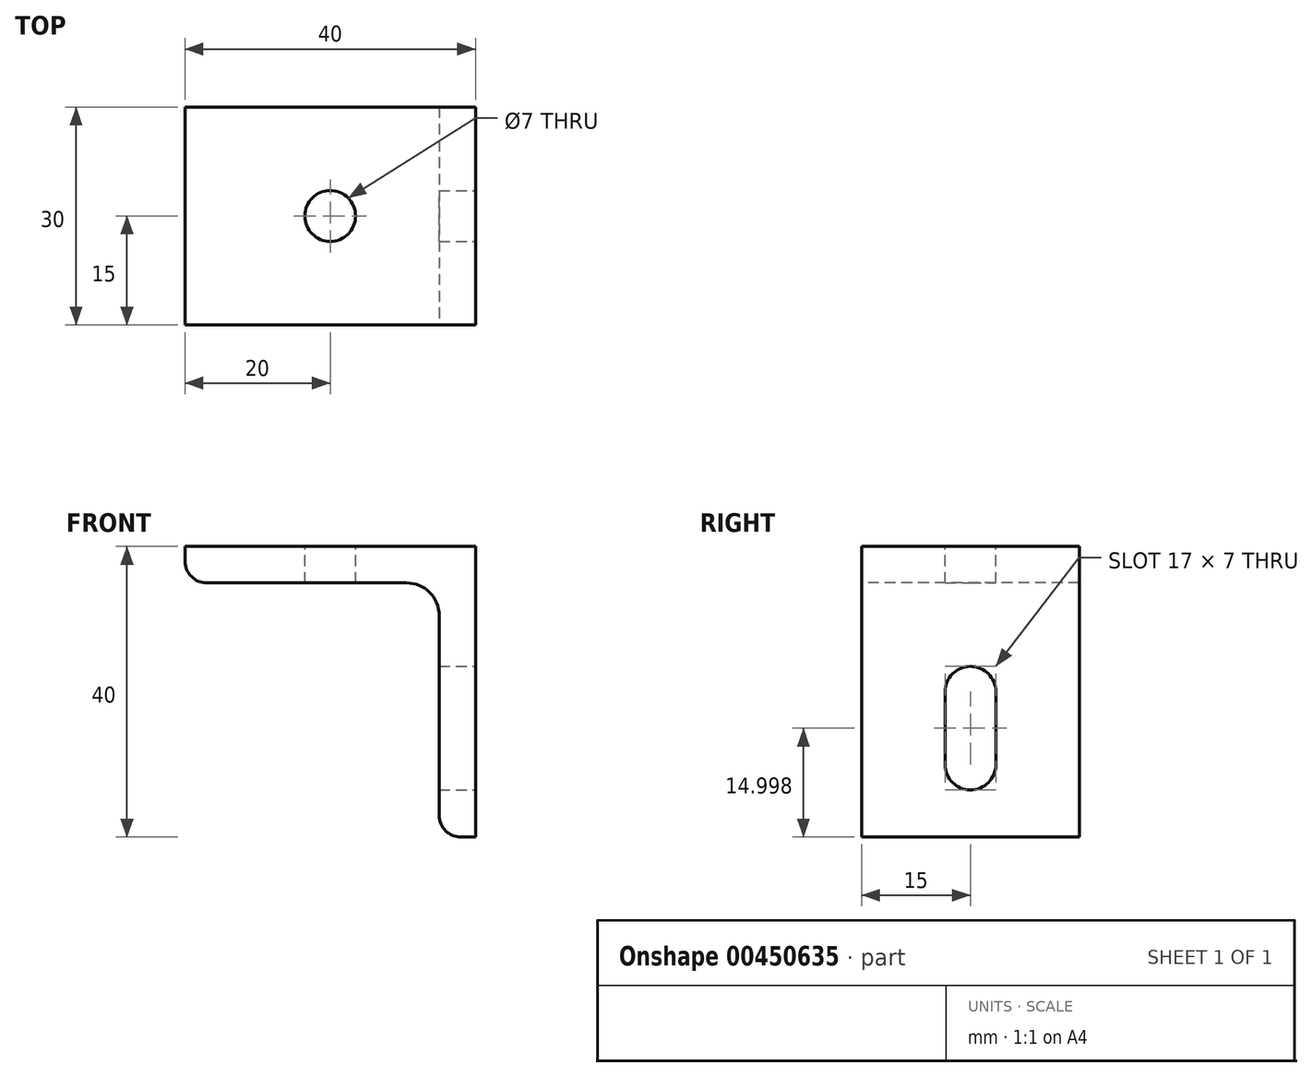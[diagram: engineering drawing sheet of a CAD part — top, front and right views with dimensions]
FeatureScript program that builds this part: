
annotation { "Feature Type Name" : "Feature", "Feature Type Description" : "" }
export const myFeature = defineFeature(function(context is Context, id is Id, definition is map)
    precondition{}
    {
        {
            var Q0;
            Q0=qCreatedBy(makeId("Front.planeOp"),FACE);
            var sketch = newSketch(context, id + "F0", { "sketchPlane" : qUnion([Q0])});
            skLineSegment(sketch, "E0", {"start": v(-170.8, -196.38) * mm, "end": v(99.2, -196.38) * mm});
            skLineSegment(sketch, "E1", {"start": v(-170.8, -169.38) * mm, "end": v(-170.8, -196.38) * mm});
            skLineSegment(sketch, "E2", {"start": v(-170.8, -169.38) * mm, "end": v(99.2, -169.38) * mm});
            skLineSegment(sketch, "E3", {"start": v(-75.8, -192.38) * mm, "end": v(-18.8, -192.38) * mm});
            skLineSegment(sketch, "E4", {"start": v(-75.8, -183.07) * mm, "end": v(-18.8, -183.07) * mm});
            skLineSegment(sketch, "E5", {"start": v(-170.8, -188.38) * mm, "end": v(-75.8, -188.38) * mm});
            skLineSegment(sketch, "E6", {"start": v(-75.8, -169.38) * mm, "end": v(-75.8, -196.38) * mm});
            skLineSegment(sketch, "E7", {"start": v(-36.8, -183.07) * mm, "end": v(-36.8, -196.38) * mm});
            skLineSegment(sketch, "E8", {"start": v(-18.8, -187.38) * mm, "end": v(99.2, -187.38) * mm});
            skLineSegment(sketch, "E9", {"start": v(26.2, -178.38) * mm, "end": v(99.2, -178.38) * mm});
            skLineSegment(sketch, "E10", {"start": v(-18.8, -174.38) * mm, "end": v(26.2, -174.38) * mm});
            skLineSegment(sketch, "E11", {"start": v(24, -176.8) * mm, "end": v(16.58, -185.84) * mm});
            skLineSegment(sketch, "E12", {"start": v(-18.8, -169.38) * mm, "end": v(-18.8, -196.38) * mm});
            skLineSegment(sketch, "E13", {"start": v(-1.8, -169.38) * mm, "end": v(-1.8, -187.38) * mm});
            skLineSegment(sketch, "E14", {"start": v(-17.86, -180.9) * mm, "end": v(-10.14, -180.9) * mm});
            skCircle(sketch, "E15", {"center": v(-14, -180.9) * mm, "radius": 2.97 * mm});
            skCircle(sketch, "E16", {"center": v(-14, -180.9) * mm, "radius": 1.47 * mm});
            skLineSegment(sketch, "E17", {"start": v(-14, -177.04) * mm, "end": v(-14, -184.77) * mm});
            skLineSegment(sketch, "E18", {"start": v(-4.04, -177.93) * mm, "end": v(-4.04, -183.87) * mm});
            skLineSegment(sketch, "E19", {"start": v(-8.12, -179.44) * mm, "end": v(-8.12, -182.37) * mm});
            skLineSegment(sketch, "E20", {"start": v(-4.04, -183.87) * mm, "end": v(-8.12, -182.37) * mm});
            skLineSegment(sketch, "E21", {"start": v(-8.95, -180.9) * mm, "end": v(-3.11, -180.9) * mm});
            skLineSegment(sketch, "E22", {"start": v(-4.04, -177.93) * mm, "end": v(-8.12, -179.44) * mm});
            skLineSegment(sketch, "E23", {"start": v(15.2, -169.38) * mm, "end": v(15.2, -187.38) * mm});
            skLineSegment(sketch, "E24", {"start": v(26.2, -169.38) * mm, "end": v(26.2, -187.38) * mm});
            skLineSegment(sketch, "E25", {"start": v(71.2, -187.38) * mm, "end": v(71.2, -196.38) * mm});
            skLineSegment(sketch, "E26", {"start": v(71.2, -169.38) * mm, "end": v(71.2, -178.38) * mm});
            skLineSegment(sketch, "E27", {"start": v(99.2, -12.38) * mm, "end": v(1.2, -12.38) * mm});
            skLineSegment(sketch, "E28", {"start": v(99.2, -18.38) * mm, "end": v(1.2, -18.38) * mm});
            skLineSegment(sketch, "E29", {"start": v(99.2, -24.38) * mm, "end": v(1.2, -24.38) * mm});
            skLineSegment(sketch, "E30", {"start": v(15.2, -6.38) * mm, "end": v(15.2, -24.38) * mm});
            skLineSegment(sketch, "E31", {"start": v(1.2, -6.38) * mm, "end": v(1.2, -24.38) * mm});
            skLineSegment(sketch, "E32", {"start": v(5.62, -11.28) * mm, "end": v(10.42, -11.28) * mm});
            skLineSegment(sketch, "E33", {"start": v(74.2, -6.38) * mm, "end": v(74.2, -24.38) * mm});
            skLineSegment(sketch, "E34", {"start": v(89.2, -6.38) * mm, "end": v(89.2, -24.38) * mm});
            skLineSegment(sketch, "E35", {"start": v(5.62, -11.28) * mm, "end": v(8.02, -7.28) * mm});
            skLineSegment(sketch, "E36", {"start": v(8.02, -7.28) * mm, "end": v(10.42, -11.28) * mm});
            skLineSegment(sketch, "E37", {"start": v(5.62, -17.28) * mm, "end": v(10.42, -17.28) * mm});
            skLineSegment(sketch, "E38", {"start": v(5.62, -17.28) * mm, "end": v(8.02, -13.28) * mm});
            skLineSegment(sketch, "E39", {"start": v(8.02, -13.28) * mm, "end": v(10.42, -17.28) * mm});
            skLineSegment(sketch, "E40", {"start": v(-170.8, -196.38) * mm, "end": v(-170.8, -6.38) * mm});
            skLineSegment(sketch, "E41", {"start": v(99.2, -196.38) * mm, "end": v(99.2, -6.38) * mm});
            skLineSegment(sketch, "E42", {"start": v(-170.8, -6.38) * mm, "end": v(99.2, -6.38) * mm});
            skLineSegment(sketch, "E43", {"start": v(144.6, -84.48) * mm, "end": v(146.05, -86.98) * mm});
            skLineSegment(sketch, "E44", {"start": v(146.05, -86.98) * mm, "end": v(149.23, -81.48) * mm});
            skLineSegment(sketch, "E45", {"start": v(149.23, -81.48) * mm, "end": v(155.58, -81.48) * mm});
            skLineSegment(sketch, "E46", {"start": v(144.6, -84.48) * mm, "end": v(147.5, -84.48) * mm});
            skLineSegment(sketch, "E47", {"start": v(157.64, -84.48) * mm, "end": v(159.08, -86.98) * mm});
            skLineSegment(sketch, "E48", {"start": v(159.08, -86.98) * mm, "end": v(162.25, -81.48) * mm});
            skCircle(sketch, "E49", {"center": v(159.08, -85.31) * mm, "radius": 0.83 * mm});
            skArc(sketch, "E50", {"start": v(144.43, -81.3) * mm, "mid": v(143.38, -84.23) * mm, "end": v(144.43, -87.15) * mm});
            skArc(sketch, "E51", {"start": v(164.29, -87.15) * mm, "mid": v(165.34, -84.23) * mm, "end": v(164.29, -81.3) * mm});
            skLineSegment(sketch, "E52", {"start": v(136.3, -188.2) * mm, "end": v(146.3, -188.2) * mm});
            skLineSegment(sketch, "E53", {"start": v(146.3, -188.2) * mm, "end": v(146.3, -178.2) * mm});
            skLineSegment(sketch, "E54", {"start": v(146.3, -178.2) * mm, "end": v(136.3, -188.2) * mm});
            skLineSegment(sketch, "E55", {"start": v(155.92, -74.84) * mm, "end": v(157.37, -77.34) * mm});
            skLineSegment(sketch, "E56", {"start": v(157.37, -77.34) * mm, "end": v(160.54, -71.84) * mm});
            skLineSegment(sketch, "E57", {"start": v(160.54, -71.84) * mm, "end": v(167.77, -71.84) * mm});
            skLineSegment(sketch, "E58", {"start": v(155.92, -74.84) * mm, "end": v(158.81, -74.84) * mm});
            skCircle(sketch, "E59", {"center": v(160.54, -71.84) * mm, "radius": 0.79 * mm});
            skLineSegment(sketch, "E60", {"start": v(153.92, -77.34) * mm, "end": v(168.92, -77.34) * mm});
            skLineSegment(sketch, "E61", {"start": v(135.86, -112.96) * mm, "end": v(137.3, -115.46) * mm});
            skLineSegment(sketch, "E62", {"start": v(137.3, -115.46) * mm, "end": v(140.48, -109.96) * mm});
            skLineSegment(sketch, "E63", {"start": v(140.48, -109.96) * mm, "end": v(147.7, -109.96) * mm});
            skLineSegment(sketch, "E64", {"start": v(135.86, -112.96) * mm, "end": v(138.75, -112.96) * mm});
            skLineSegment(sketch, "E65", {"start": v(135.86, -122.83) * mm, "end": v(137.3, -125.33) * mm});
            skLineSegment(sketch, "E66", {"start": v(137.3, -125.33) * mm, "end": v(140.48, -119.83) * mm});
            skLineSegment(sketch, "E67", {"start": v(140.48, -119.83) * mm, "end": v(147.7, -119.83) * mm});
            skLineSegment(sketch, "E68", {"start": v(135.86, -122.83) * mm, "end": v(138.75, -122.83) * mm});
            skLineSegment(sketch, "E69", {"start": v(135.77, -132.54) * mm, "end": v(137.22, -135.04) * mm});
            skLineSegment(sketch, "E70", {"start": v(137.22, -135.04) * mm, "end": v(140.4, -129.54) * mm});
            skLineSegment(sketch, "E71", {"start": v(140.4, -129.54) * mm, "end": v(146.74, -129.54) * mm});
            skLineSegment(sketch, "E72", {"start": v(135.77, -132.54) * mm, "end": v(138.66, -132.54) * mm});
            skLineSegment(sketch, "E73", {"start": v(135.92, -141.53) * mm, "end": v(137.37, -144.03) * mm});
            skLineSegment(sketch, "E74", {"start": v(137.37, -144.03) * mm, "end": v(140.54, -138.53) * mm});
            skLineSegment(sketch, "E75", {"start": v(140.54, -138.53) * mm, "end": v(146.92, -138.53) * mm});
            skLineSegment(sketch, "E76", {"start": v(135.92, -141.53) * mm, "end": v(138.81, -141.53) * mm});
            skLineSegment(sketch, "E77", {"start": v(135.92, -150.24) * mm, "end": v(137.37, -152.74) * mm});
            skLineSegment(sketch, "E78", {"start": v(137.37, -152.74) * mm, "end": v(140.54, -147.24) * mm});
            skLineSegment(sketch, "E79", {"start": v(140.54, -147.24) * mm, "end": v(146.92, -147.24) * mm});
            skLineSegment(sketch, "E80", {"start": v(135.92, -150.24) * mm, "end": v(138.81, -150.24) * mm});
            skLineSegment(sketch, "E81", {"start": v(136.89, -26.68) * mm, "end": v(138.33, -29.18) * mm});
            skLineSegment(sketch, "E82", {"start": v(138.33, -29.18) * mm, "end": v(141.5, -23.68) * mm});
            skLineSegment(sketch, "E83", {"start": v(141.5, -23.68) * mm, "end": v(148.73, -23.68) * mm});
            skLineSegment(sketch, "E84", {"start": v(136.89, -26.68) * mm, "end": v(139.77, -26.68) * mm});
            skLineSegment(sketch, "E85", {"start": v(134.88, -29.18) * mm, "end": v(149.88, -29.18) * mm});
            skLineSegment(sketch, "E86", {"start": v(136.89, -36.55) * mm, "end": v(138.33, -39.05) * mm});
            skLineSegment(sketch, "E87", {"start": v(138.33, -39.05) * mm, "end": v(141.5, -33.55) * mm});
            skLineSegment(sketch, "E88", {"start": v(141.5, -33.55) * mm, "end": v(148.73, -33.55) * mm});
            skLineSegment(sketch, "E89", {"start": v(136.89, -36.55) * mm, "end": v(139.77, -36.55) * mm});
            skLineSegment(sketch, "E90", {"start": v(134.88, -39.05) * mm, "end": v(149.88, -39.05) * mm});
            skLineSegment(sketch, "E91", {"start": v(136.8, -46.27) * mm, "end": v(138.24, -48.77) * mm});
            skLineSegment(sketch, "E92", {"start": v(138.24, -48.77) * mm, "end": v(141.42, -43.27) * mm});
            skLineSegment(sketch, "E93", {"start": v(141.42, -43.27) * mm, "end": v(147.76, -43.27) * mm});
            skLineSegment(sketch, "E94", {"start": v(136.8, -46.27) * mm, "end": v(139.68, -46.27) * mm});
            skLineSegment(sketch, "E95", {"start": v(134.8, -48.77) * mm, "end": v(149.8, -48.77) * mm});
            skLineSegment(sketch, "E96", {"start": v(136.95, -55.25) * mm, "end": v(138.4, -57.75) * mm});
            skLineSegment(sketch, "E97", {"start": v(138.4, -57.75) * mm, "end": v(141.57, -52.25) * mm});
            skLineSegment(sketch, "E98", {"start": v(141.57, -52.25) * mm, "end": v(147.95, -52.25) * mm});
            skLineSegment(sketch, "E99", {"start": v(136.95, -55.25) * mm, "end": v(139.83, -55.25) * mm});
            skLineSegment(sketch, "E100", {"start": v(134.94, -57.75) * mm, "end": v(149.94, -57.75) * mm});
            skLineSegment(sketch, "E101", {"start": v(136.95, -63.96) * mm, "end": v(138.4, -66.46) * mm});
            skLineSegment(sketch, "E102", {"start": v(138.4, -66.46) * mm, "end": v(141.57, -60.96) * mm});
            skLineSegment(sketch, "E103", {"start": v(141.57, -60.96) * mm, "end": v(147.95, -60.96) * mm});
            skLineSegment(sketch, "E104", {"start": v(136.95, -63.96) * mm, "end": v(139.83, -63.96) * mm});
            skLineSegment(sketch, "E105", {"start": v(134.88, -66.36) * mm, "end": v(149.88, -66.36) * mm});
            skLineSegment(sketch, "E106", {"start": v(137.15, -84.48) * mm, "end": v(138.6, -86.98) * mm});
            skLineSegment(sketch, "E107", {"start": v(138.6, -86.98) * mm, "end": v(141.77, -81.48) * mm});
            skLineSegment(sketch, "E108", {"start": v(137.56, -74.63) * mm, "end": v(139, -77.13) * mm});
            skLineSegment(sketch, "E109", {"start": v(139, -77.13) * mm, "end": v(142.18, -71.63) * mm});
            skCircle(sketch, "E110", {"center": v(139, -75.47) * mm, "radius": 0.83 * mm});
            skLineSegment(sketch, "E111", {"start": v(136, -77.13) * mm, "end": v(143, -77.13) * mm});
            skLineSegment(sketch, "E112", {"start": v(146.86, -74.84) * mm, "end": v(148.3, -77.34) * mm});
            skLineSegment(sketch, "E113", {"start": v(148.3, -77.34) * mm, "end": v(151.48, -71.84) * mm});
            skLineSegment(sketch, "E114", {"start": v(146.86, -74.84) * mm, "end": v(149.74, -74.84) * mm});
            skLineSegment(sketch, "E115", {"start": v(145.3, -77.34) * mm, "end": v(152.3, -77.34) * mm});
            skLineSegment(sketch, "E116", {"start": v(136.3, -93.03) * mm, "end": v(137.75, -95.53) * mm});
            skLineSegment(sketch, "E117", {"start": v(137.75, -95.53) * mm, "end": v(140.93, -90.03) * mm});
            skLineSegment(sketch, "E118", {"start": v(141.75, -95.53) * mm, "end": v(134.75, -95.53) * mm});
            skLineSegment(sketch, "E119", {"start": v(157.93, -63.96) * mm, "end": v(159.38, -66.46) * mm});
            skLineSegment(sketch, "E120", {"start": v(159.38, -66.46) * mm, "end": v(162.55, -60.96) * mm});
            skLineSegment(sketch, "E121", {"start": v(162.55, -60.96) * mm, "end": v(168.93, -60.96) * mm});
            skLineSegment(sketch, "E122", {"start": v(157.93, -63.96) * mm, "end": v(160.82, -63.96) * mm});
            skLineSegment(sketch, "E123", {"start": v(155.87, -66.36) * mm, "end": v(170.87, -66.36) * mm});
            skLineSegment(sketch, "E124", {"start": v(157.93, -151.56) * mm, "end": v(159.38, -154.06) * mm});
            skLineSegment(sketch, "E125", {"start": v(159.38, -154.06) * mm, "end": v(162.55, -148.56) * mm});
            skLineSegment(sketch, "E126", {"start": v(162.55, -148.56) * mm, "end": v(168.93, -148.56) * mm});
            skLineSegment(sketch, "E127", {"start": v(157.93, -151.56) * mm, "end": v(160.82, -151.56) * mm});
            skLineSegment(sketch, "E128", {"start": v(145.83, -161.12) * mm, "end": v(147.28, -163.62) * mm});
            skLineSegment(sketch, "E129", {"start": v(147.28, -163.62) * mm, "end": v(150.45, -158.12) * mm});
            skLineSegment(sketch, "E130", {"start": v(145.83, -161.12) * mm, "end": v(148.72, -161.12) * mm});
            skLineSegment(sketch, "E131", {"start": v(136.53, -160.9) * mm, "end": v(137.98, -163.4) * mm});
            skLineSegment(sketch, "E132", {"start": v(137.98, -163.4) * mm, "end": v(141.15, -157.9) * mm});
            skCircle(sketch, "E133", {"center": v(137.98, -161.74) * mm, "radius": 0.83 * mm});
            skLineSegment(sketch, "E134", {"start": v(-72, -178.14) * mm, "end": v(-70.55, -180.64) * mm});
            skLineSegment(sketch, "E135", {"start": v(-70.55, -180.64) * mm, "end": v(-67.37, -175.14) * mm});
            skLineSegment(sketch, "E136", {"start": v(-60.61, -177.93) * mm, "end": v(-59.17, -180.43) * mm});
            skLineSegment(sketch, "E137", {"start": v(-59.17, -180.43) * mm, "end": v(-56, -174.93) * mm});
            skCircle(sketch, "E138", {"center": v(-59.17, -178.76) * mm, "radius": 0.83 * mm});
            skArc(sketch, "E139", {"start": v(-75.97, -110.64) * mm, "mid": v(-77.52, -107.99) * mm, "end": v(-80.4, -106.94) * mm});
            skArc(sketch, "E140", {"start": v(-75.9, -111.44) * mm, "mid": v(-75.92, -111.04) * mm, "end": v(-75.97, -110.64) * mm});
            skLineSegment(sketch, "E141", {"start": v(-80.4, -106.94) * mm, "end": v(-107.9, -106.94) * mm});
            skLineSegment(sketch, "E142", {"start": v(-75.9, -138.94) * mm, "end": v(-75.9, -111.44) * mm});
            skArc(sketch, "E143", {"start": v(-110.9, -103.94) * mm, "mid": v(-110.02, -106.06) * mm, "end": v(-107.9, -106.94) * mm});
            skLineSegment(sketch, "E144", {"start": v(-110.9, -103.94) * mm, "end": v(-110.9, -101.94) * mm});
            skArc(sketch, "E145", {"start": v(-75.9, -138.94) * mm, "mid": v(-75.02, -141.06) * mm, "end": v(-72.9, -141.94) * mm});
            skLineSegment(sketch, "E146", {"start": v(-70.9, -141.94) * mm, "end": v(-72.9, -141.94) * mm});
            skLineSegment(sketch, "E147", {"start": v(-70.9, -141.94) * mm, "end": v(-70.9, -101.94) * mm});
            skLineSegment(sketch, "E148", {"start": v(-70.9, -101.94) * mm, "end": v(-110.9, -101.94) * mm});
            skLineSegment(sketch, "E149", {"start": v(37.15, -106.94) * mm, "end": v(7.15, -106.94) * mm});
            skLineSegment(sketch, "E150", {"start": v(7.15, -139.94) * mm, "end": v(7.15, -101.94) * mm});
            skLineSegment(sketch, "E151", {"start": v(9.15, -141.94) * mm, "end": v(7.15, -139.94) * mm});
            skLineSegment(sketch, "E152", {"start": v(35.15, -141.94) * mm, "end": v(9.15, -141.94) * mm});
            skLineSegment(sketch, "E153", {"start": v(37.15, -139.94) * mm, "end": v(35.15, -141.94) * mm});
            skArc(sketch, "E154", {"start": v(18.65, -131.94) * mm, "mid": v(22.15, -135.44) * mm, "end": v(25.65, -131.94) * mm});
            skArc(sketch, "E155", {"start": v(25.65, -121.94) * mm, "mid": v(22.15, -118.44) * mm, "end": v(18.65, -121.94) * mm});
            skLineSegment(sketch, "E156", {"start": v(17.6, -131.94) * mm, "end": v(26.7, -131.94) * mm});
            skLineSegment(sketch, "E157", {"start": v(17.6, -121.94) * mm, "end": v(26.7, -121.94) * mm});
            skLineSegment(sketch, "E158", {"start": v(18.65, -121.94) * mm, "end": v(18.65, -131.94) * mm});
            skLineSegment(sketch, "E159", {"start": v(25.65, -131.94) * mm, "end": v(25.65, -121.94) * mm});
            skLineSegment(sketch, "E160", {"start": v(37.15, -139.94) * mm, "end": v(37.15, -101.94) * mm});
            skLineSegment(sketch, "E161", {"start": v(7.15, -101.94) * mm, "end": v(37.15, -101.94) * mm});
            skLineSegment(sketch, "E162", {"start": v(-75.9, -55.1) * mm, "end": v(-75.9, -25.1) * mm});
            skLineSegment(sketch, "E163", {"start": v(-108.9, -25.1) * mm, "end": v(-70.9, -25.1) * mm});
            skLineSegment(sketch, "E164", {"start": v(-110.9, -53.1) * mm, "end": v(-110.9, -27.1) * mm});
            skLineSegment(sketch, "E165", {"start": v(-108.9, -25.1) * mm, "end": v(-110.9, -27.1) * mm});
            skLineSegment(sketch, "E166", {"start": v(-108.9, -55.1) * mm, "end": v(-110.9, -53.1) * mm});
            skLineSegment(sketch, "E167", {"start": v(-90.9, -35.56) * mm, "end": v(-90.9, -44.66) * mm});
            skLineSegment(sketch, "E168", {"start": v(-108.9, -55.1) * mm, "end": v(-70.9, -55.1) * mm});
            skLineSegment(sketch, "E169", {"start": v(-70.9, -25.1) * mm, "end": v(-70.9, -55.1) * mm});
            skLineSegment(sketch, "E170", {"start": v(22.15, -117.4) * mm, "end": v(22.15, -136.5) * mm});
            skLineSegment(sketch, "E171", {"start": v(-86.35, -40.1) * mm, "end": v(-95.45, -40.1) * mm});
            skCircle(sketch, "E172", {"center": v(-90.9, -40.1) * mm, "radius": 3.5 * mm});
            skLineSegment(sketch, "E173", {"start": v(-61.22, -99.44) * mm, "end": v(-59.78, -101.94) * mm});
            skLineSegment(sketch, "E174", {"start": v(-59.78, -101.94) * mm, "end": v(-56.6, -96.44) * mm});
            skCircle(sketch, "E175", {"center": v(-59.78, -100.28) * mm, "radius": 0.83 * mm});
            skLineSegment(sketch, "E176", {"start": v(-56.6, -96.44) * mm, "end": v(-51.76, -96.44) * mm});
            skCircle(sketch, "E177", {"center": v(-56.6, -96.44) * mm, "radius": 0.79 * mm});
            skLineSegment(sketch, "E178", {"start": v(-56, -174.93) * mm, "end": v(-51.06, -174.93) * mm});
            skCircle(sketch, "E179", {"center": v(-56, -174.93) * mm, "radius": 0.79 * mm});
            skLineSegment(sketch, "E180", {"start": v(44.07, -108.99) * mm, "end": v(45.5, -111.49) * mm});
            skLineSegment(sketch, "E181", {"start": v(45.5, -111.49) * mm, "end": v(48.69, -105.99) * mm});
            skLineSegment(sketch, "E182", {"start": v(48.69, -105.99) * mm, "end": v(55.9, -105.99) * mm});
            skLineSegment(sketch, "E183", {"start": v(44.07, -108.99) * mm, "end": v(46.95, -108.99) * mm});
            skLineSegment(sketch, "E184", {"start": v(42.06, -111.49) * mm, "end": v(57.06, -111.49) * mm});
            skCircle(sketch, "E185", {"center": v(48.69, -105.99) * mm, "radius": 0.79 * mm});
            skLineSegment(sketch, "E186", {"start": v(45.13, -68.73) * mm, "end": v(46.57, -71.23) * mm});
            skLineSegment(sketch, "E187", {"start": v(46.57, -71.23) * mm, "end": v(49.75, -65.73) * mm});
            skLineSegment(sketch, "E188", {"start": v(49.75, -65.73) * mm, "end": v(56.1, -65.73) * mm});
            skLineSegment(sketch, "E189", {"start": v(45.13, -68.73) * mm, "end": v(48.01, -68.73) * mm});
            skLineSegment(sketch, "E190", {"start": v(43.12, -71.23) * mm, "end": v(58.12, -71.23) * mm});
            skLineSegment(sketch, "E191", {"start": v(-11.48, -69.53) * mm, "end": v(-10.04, -72.03) * mm});
            skLineSegment(sketch, "E192", {"start": v(-10.04, -72.03) * mm, "end": v(-6.86, -66.53) * mm});
            skLineSegment(sketch, "E193", {"start": v(-6.86, -66.53) * mm, "end": v(-0.52, -66.53) * mm});
            skLineSegment(sketch, "E194", {"start": v(-11.48, -69.53) * mm, "end": v(-8.6, -69.53) * mm});
            skLineSegment(sketch, "E195", {"start": v(-13.49, -72.03) * mm, "end": v(1.51, -72.03) * mm});
            skLineSegment(sketch, "E196", {"start": v(-49.5, -178.24) * mm, "end": v(-48.05, -180.74) * mm});
            skLineSegment(sketch, "E197", {"start": v(-48.05, -180.74) * mm, "end": v(-44.88, -175.24) * mm});
            skLineSegment(sketch, "E198", {"start": v(-44.88, -175.24) * mm, "end": v(-37.66, -175.24) * mm});
            skLineSegment(sketch, "E199", {"start": v(-49.5, -178.24) * mm, "end": v(-46.61, -178.24) * mm});
            skLineSegment(sketch, "E200", {"start": v(-36.54, -178.43) * mm, "end": v(-35.1, -180.93) * mm});
            skLineSegment(sketch, "E201", {"start": v(-35.1, -180.93) * mm, "end": v(-31.93, -175.43) * mm});
            skLineSegment(sketch, "E202", {"start": v(-31.93, -175.43) * mm, "end": v(-25.58, -175.43) * mm});
            skLineSegment(sketch, "E203", {"start": v(-36.54, -178.43) * mm, "end": v(-33.66, -178.43) * mm});
            skSolve(sketch);
        }
        {
            var Q0;
            Q0=makeQuery(id+"F0.imprint","IMPRINT",FACE,{"disambiguationData":[TD([[makeQuery(id+"F0.imprint","IMPRINT",EDGE,{"derivedFrom":sQuery(id+"F0.wireOp",EDGE,"E139")}),-1.0]])]});
            extrude(context, id + "F1", {"entities" : qUnion([Q0]), "oppositeDirection" : true, "depth" : 30 * mm});
        }
        {
            var Q0;
            Q0=makeQuery(id+"F1.opExtrude","SWEPT_FACE",FACE,{"disambiguationData":[OSD([sQuery(id+"F0.wireOp",EDGE,"E148")])]});
            var sketch = newSketch(context, id + "F2", { "sketchPlane" : qUnion([Q0])});
            skPoint(sketch, "E204", {"position": v(-90.9, 15) * mm});
            skSolve(sketch);
        }
        {
            var Q0;
            Q0=sQuery(id+"F2.wireOp",VERTEX,"E204");
            var Q1;
            Q1=makeQuery(id+"F1.opExtrude","SWEPT_BODY",BODY,{"disambiguationData":[OSD([sQuery(id+"F0.wireOp",EDGE,"E139"),sQuery(id+"F0.wireOp",EDGE,"E140"),sQuery(id+"F0.wireOp",EDGE,"E141"),sQuery(id+"F0.wireOp",EDGE,"E142"),sQuery(id+"F0.wireOp",EDGE,"E143"),sQuery(id+"F0.wireOp",EDGE,"E144"),sQuery(id+"F0.wireOp",EDGE,"E145"),sQuery(id+"F0.wireOp",EDGE,"E146"),sQuery(id+"F0.wireOp",EDGE,"E147"),sQuery(id+"F0.wireOp",EDGE,"E148")])]});
            hole(context, id + "F3", {"style" : HoleStyle.SIMPLE, "endStyle" : HoleEndStyle.THROUGH, "holeDiameter" : 7 * mm, "isTappedThrough" : true, "tappedDepth" : 12 * mm, "tapClearance" : 3, "locations" : qUnion([Q0]), "scope" : qUnion([Q1])});
        }
        {
            var Q0;
            Q0=makeQuery(id+"F1.opExtrude","SWEPT_FACE",FACE,{"disambiguationData":[OSD([sQuery(id+"F0.wireOp",EDGE,"E147")])]});
            var sketch = newSketch(context, id + "F4", { "sketchPlane" : qUnion([Q0])});
            skLineSegment(sketch, "E205.0", {"start": v(18.5, -131.94) * mm, "end": v(18.5, -121.94) * mm});
            skArc(sketch, "E206", {"start": v(18.5, -121.94) * mm, "mid": v(15, -118.44) * mm, "end": v(11.5, -121.94) * mm});
            skArc(sketch, "E207", {"start": v(11.5, -131.94) * mm, "mid": v(15, -135.44) * mm, "end": v(18.5, -131.94) * mm});
            skLineSegment(sketch, "E208.0", {"start": v(11.5, -131.94) * mm, "end": v(11.5, -121.94) * mm});
            skSolve(sketch);
        }
        {
            var Q0;
            Q0 = qSketchRegion(id + "F4", true);
            extrude(context, id + "F5", {"entities" : qUnion([Q0]), "operationType" : NewBodyOperationType.REMOVE, "oppositeDirection" : true, "depth" : 25 * mm});
        }
    });
